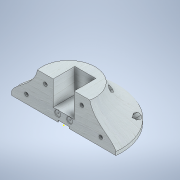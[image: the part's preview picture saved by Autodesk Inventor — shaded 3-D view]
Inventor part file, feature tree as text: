
AUTODESK INVENTOR PART (.ipt)
format: ipt  version: 2021 (Build 250183000, 183)  size: 326,144 bytes
history: native  units: mm
features: sketch x9, extrude x7, plane x2, revolve x1, split x1
ambient origin geometry x8: Origin, YZ Plane, XZ Plane, XY Plane, X Axis, Y Axis, Z Axis, Center Point
bodies: Solid1 (feature_tree)
feature tree (20):
  revolve  "Revolution1"  [1 undecoded]
  extrude  "Extrusion1"  Depth=5.0mm
  extrude  "Extrusion2"  Depth=30.0mm
  extrude  "Extrusion3"  Depth=24.0mm
  plane  "Work Plane1"
  split  "Split1"
  extrude  "Extrusion4"  Depth=35.0mm TaperAngle=0.0deg
  plane  "Work Plane2"
  extrude  "Extrusion5"  Depth=8.0mm TaperAngle=0.0deg
  sketch  "Sketch8"  dims[d14=5.2mm d15=5.2mm]
  extrude  "Extrusion6"  Depth=5.2mm
  extrude  "Extrusion7"  Depth=12.0mm
  sketch  "Sketch1"  dims[d0=75.0mm d1=50.0mm]
  sketch  "Sketch2"  dims[d2=38.0mm d3=5.0mm]
  sketch  "Sketch3"  dims[d4=90.0deg d5=30.0mm]
  sketch  "Sketch4"  dims[d6=48.0mm d7=24.0mm]
  sketch  "Sketch6"  dims[d8=15.0mm d9=35.0mm d10=0.0mm]
  sketch  "Sketch7"  dims[d11=17.0mm d12=8.0mm d13=0.0mm]
  sketch  "Sketch9"  dims[d16=12.0mm d17=12.0mm]
  sketch  "Sketch10"  dims[d18=22.0mm d19=12.0mm d20=52.0mm d21=52.0mm d22=0.0mm d23=0.0mm d24=0.0mm d25=21.0mm d26=2.5mm d27=0.0mm d28=-12.5mm d29=8.0mm d30=8.0mm d31=8.0mm d32=8.0mm d33=50.0mm d34=0.0mm d35=8.5mm d36=8.5mm d37=1.0mm d38=0.0mm d39=1.5mm d40=1.5mm d41=10.0mm d42=0.0mm]
note: 1 required parameter value undecoded (feature->parameter linkage not recoverable at this tier; creation-order binding heuristic only, values carry confidence <= 0.55)
